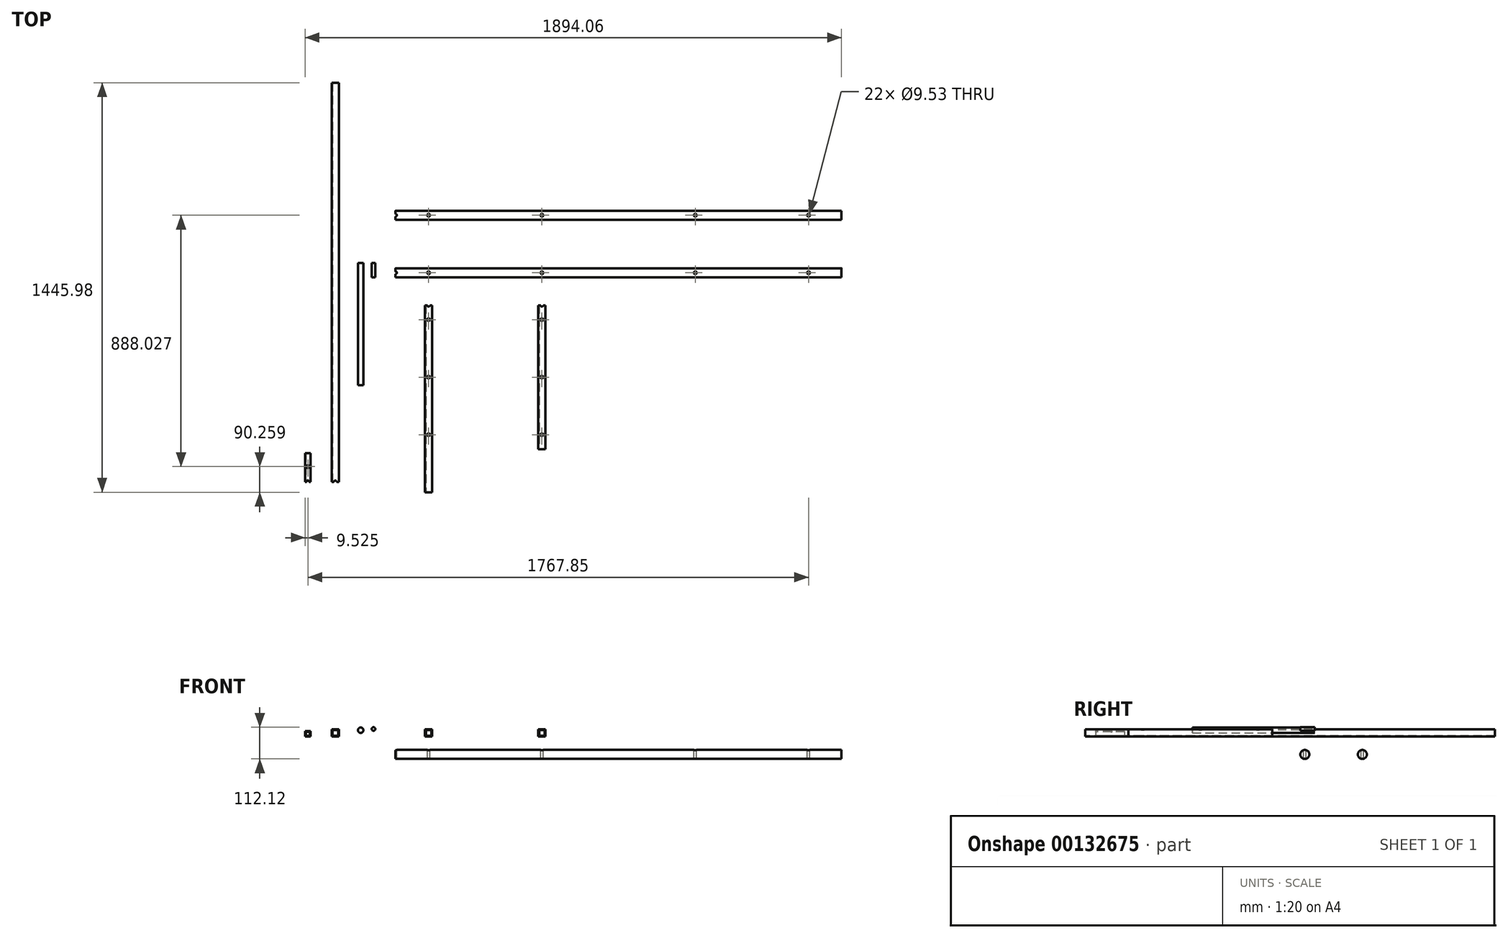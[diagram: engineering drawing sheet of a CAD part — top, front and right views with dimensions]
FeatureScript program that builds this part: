
annotation { "Feature Type Name" : "Feature", "Feature Type Description" : "" }
export const myFeature = defineFeature(function(context is Context, id is Id, definition is map)
    precondition{}
    {
        {
            var Q0;
            Q0=qCreatedBy(makeId("Right.planeOp"),FACE);
            var sketch = newSketch(context, id + "F0", { "sketchPlane" : qUnion([Q0])});
            skCircle(sketch, "E0", {"center": v(-35.07, -63.12) * mm, "radius": 15.88 * mm});
            skCircle(sketch, "E1", {"center": v(168.13, -63.12) * mm, "radius": 15.88 * mm});
            skSolve(sketch);
        }
        {
            var Q0;
            Q0=makeQuery(id+"F0.imprint","IMPRINT",FACE,{"disambiguationData":[TD([[makeQuery(id+"F0.imprint","IMPRINT",EDGE,{"derivedFrom":sQuery(id+"F0.wireOp",EDGE,"E1")}),1.0]])]});
            var Q1;
            Q1=makeQuery(id+"F0.imprint","IMPRINT",FACE,{"disambiguationData":[TD([[makeQuery(id+"F0.imprint","IMPRINT",EDGE,{"derivedFrom":sQuery(id+"F0.wireOp",EDGE,"E0")}),1.0]])]});
            extrude(context, id + "F1", {"entities" : qUnion([Q0, Q1]), "depth" : 1574.8 * mm});
        }
        {
            var Q0;
            Q0=qCreatedBy(makeId("Top.planeOp"),FACE);
            var sketch = newSketch(context, id + "F2", { "sketchPlane" : qUnion([Q0])});
            skPoint(sketch, "E2", {"position": v(0, -35.07) * mm});
            skPoint(sketch, "E3", {"position": v(116.68, -35.07) * mm});
            skPoint(sketch, "E4", {"position": v(1458.12, -35.07) * mm});
            skPoint(sketch, "E5", {"position": v(516.73, -35.07) * mm});
            skPoint(sketch, "E6", {"position": v(1058.07, -35.07) * mm});
            skPoint(sketch, "E7", {"position": v(116.68, 168.13) * mm});
            skPoint(sketch, "E8", {"position": v(0, 168.13) * mm});
            skPoint(sketch, "E9", {"position": v(516.73, 168.13) * mm});
            skPoint(sketch, "E10", {"position": v(1058.07, 168.13) * mm});
            skPoint(sketch, "E11", {"position": v(1458.12, 168.13) * mm});
            skSolve(sketch);
        }
        {
            var Q0;
            Q0=sQuery(id+"F2.wireOp",VERTEX,"E3");
            var Q1;
            Q1=sQuery(id+"F2.wireOp",VERTEX,"E4");
            var Q2;
            Q2=sQuery(id+"F2.wireOp",VERTEX,"E5");
            var Q3;
            Q3=sQuery(id+"F2.wireOp",VERTEX,"E6");
            var Q4;
            Q4=sQuery(id+"F2.wireOp",VERTEX,"E7");
            var Q5;
            Q5=sQuery(id+"F2.wireOp",VERTEX,"E9");
            var Q6;
            Q6=sQuery(id+"F2.wireOp",VERTEX,"E10");
            var Q7;
            Q7=sQuery(id+"F2.wireOp",VERTEX,"E11");
            var Q8;
            Q8=sQuery(id+"F2.wireOp",VERTEX,"E8");
            var Q9;
            Q9=sQuery(id+"F2.wireOp",VERTEX,"E2");
            var Q10;
            Q10=makeQuery(id+"F1.opExtrude","SWEPT_BODY",BODY,{"disambiguationData":[OSD([sQuery(id+"F0.wireOp",EDGE,"E0")])]});
            var Q11;
            Q11=makeQuery(id+"F1.opExtrude","SWEPT_BODY",BODY,{"disambiguationData":[OSD([sQuery(id+"F0.wireOp",EDGE,"E1")])]});
            hole(context, id + "F3", {"style" : HoleStyle.SIMPLE, "endStyle" : HoleEndStyle.THROUGH, "holeDiameter" : 9.52 * mm, "startFromSketch" : true, "locations" : qUnion([Q0, Q1, Q2, Q3, Q4, Q5, Q6, Q7, Q8, Q9]), "scope" : qUnion([Q10, Q11]), "isTappedThrough" : true});
        }
        {
            var Q0;
            Q0=qCreatedBy(makeId("Top.planeOp"),FACE);
            var sketch = newSketch(context, id + "F4", { "sketchPlane" : qUnion([Q0])});
            skLineSegment(sketch, "E12.bottom", {"start": v(103.98, -149.76) * mm, "end": v(129.38, -149.76) * mm});
            skLineSegment(sketch, "E12.top", {"start": v(103.98, -810.16) * mm, "end": v(129.38, -810.16) * mm});
            skLineSegment(sketch, "E12.left", {"start": v(103.98, -149.76) * mm, "end": v(103.98, -810.16) * mm});
            skLineSegment(sketch, "E12.right", {"start": v(129.38, -149.76) * mm, "end": v(129.38, -810.16) * mm});
            skPoint(sketch, "E13", {"position": v(116.68, -149.76) * mm});
            skLineSegment(sketch, "E14.bottom", {"start": v(504.03, -149.76) * mm, "end": v(529.43, -149.76) * mm});
            skLineSegment(sketch, "E14.top", {"start": v(504.03, -657.76) * mm, "end": v(529.43, -657.76) * mm});
            skLineSegment(sketch, "E14.left", {"start": v(504.03, -149.76) * mm, "end": v(504.03, -657.76) * mm});
            skLineSegment(sketch, "E14.right", {"start": v(529.43, -149.76) * mm, "end": v(529.43, -657.76) * mm});
            skPoint(sketch, "E15", {"position": v(516.73, -149.76) * mm});
            skPoint(sketch, "E16", {"position": v(116.68, -200.56) * mm});
            skPoint(sketch, "E17", {"position": v(116.68, -403.76) * mm});
            skPoint(sketch, "E18", {"position": v(116.68, -606.96) * mm});
            skPoint(sketch, "E19", {"position": v(516.73, -200.56) * mm});
            skPoint(sketch, "E20", {"position": v(516.73, -403.76) * mm});
            skPoint(sketch, "E21", {"position": v(516.73, -606.96) * mm});
            skSolve(sketch);
        }
        {
            var Q0;
            Q0=makeQuery(id+"F4.imprint","IMPRINT",FACE,{"disambiguationData":[TD([[makeQuery(id+"F4.imprint","IMPRINT",EDGE,{"derivedFrom":sQuery(id+"F4.wireOp",EDGE,"E12.bottom")}),-1.0]])]});
            extrude(context, id + "F5", {"entities" : qUnion([Q0]), "depth" : 25.4 * mm});
        }
        {
            var Q0;
            Q0=makeQuery(id+"F4.imprint","IMPRINT",FACE,{"disambiguationData":[TD([[makeQuery(id+"F4.imprint","IMPRINT",EDGE,{"derivedFrom":sQuery(id+"F4.wireOp",EDGE,"E14.bottom")}),-1.0]])]});
            extrude(context, id + "F6", {"entities" : qUnion([Q0]), "depth" : 25.4 * mm});
        }
        {
            var Q0;
            Q0=makeQuery(id+"F5.opExtrude","SWEPT_FACE",FACE,{"disambiguationData":[OSD([sQuery(id+"F4.wireOp",EDGE,"E12.top")])]});
            var sketch = newSketch(context, id + "F7", { "sketchPlane" : qUnion([Q0])});
            skLineSegment(sketch, "E22.bottom", {"start": v(106.78, 22.6) * mm, "end": v(126.59, 22.6) * mm});
            skLineSegment(sketch, "E22.top", {"start": v(106.78, 2.8) * mm, "end": v(126.59, 2.8) * mm});
            skLineSegment(sketch, "E22.left", {"start": v(106.78, 22.6) * mm, "end": v(106.78, 2.8) * mm});
            skLineSegment(sketch, "E22.right", {"start": v(126.59, 22.6) * mm, "end": v(126.59, 2.8) * mm});
            skLineSegment(sketch, "E23.bottom", {"start": v(506.83, 22.6) * mm, "end": v(526.64, 22.6) * mm});
            skLineSegment(sketch, "E23.top", {"start": v(506.83, 2.8) * mm, "end": v(526.64, 2.8) * mm});
            skLineSegment(sketch, "E23.left", {"start": v(506.83, 22.6) * mm, "end": v(506.83, 2.8) * mm});
            skLineSegment(sketch, "E23.right", {"start": v(526.64, 22.6) * mm, "end": v(526.64, 2.8) * mm});
            skSolve(sketch);
        }
        {
            var Q0;
            Q0=makeQuery(id+"F7.imprint","IMPRINT",FACE,{"disambiguationData":[TD([[makeQuery(id+"F7.imprint","IMPRINT",EDGE,{"derivedFrom":sQuery(id+"F7.wireOp",EDGE,"E22.bottom")}),-1.0]])]});
            extrude(context, id + "F8", {"entities" : qUnion([Q0]), "operationType" : NewBodyOperationType.REMOVE, "oppositeDirection" : true, "depth" : 660.4 * mm});
        }
        {
            var Q0;
            Q0=makeQuery(id+"F7.imprint","IMPRINT",FACE,{"disambiguationData":[TD([[makeQuery(id+"F7.imprint","IMPRINT",EDGE,{"derivedFrom":sQuery(id+"F7.wireOp",EDGE,"E23.bottom")}),-1.0]])]});
            extrude(context, id + "F9", {"entities" : qUnion([Q0]), "operationType" : NewBodyOperationType.REMOVE, "oppositeDirection" : true, "depth" : 660.4 * mm});
        }
        {
            var Q0;
            Q0=sQuery(id+"F4.wireOp",VERTEX,"E13");
            var Q1;
            Q1=sQuery(id+"F4.wireOp",VERTEX,"E16");
            var Q2;
            Q2=sQuery(id+"F4.wireOp",VERTEX,"E17");
            var Q3;
            Q3=sQuery(id+"F4.wireOp",VERTEX,"E18");
            var Q4;
            Q4=makeQuery(id+"F5.opExtrude","SWEPT_BODY",BODY,{"disambiguationData":[OSD([sQuery(id+"F4.wireOp",EDGE,"E12.bottom"),sQuery(id+"F4.wireOp",EDGE,"E12.top"),sQuery(id+"F4.wireOp",EDGE,"E12.left"),sQuery(id+"F4.wireOp",EDGE,"E12.right")])]});
            hole(context, id + "F10", {"style" : HoleStyle.SIMPLE, "endStyle" : HoleEndStyle.THROUGH, "oppositeDirection" : true, "holeDiameter" : 9.52 * mm, "startFromSketch" : true, "locations" : qUnion([Q0, Q1, Q2, Q3]), "scope" : qUnion([Q4]), "isTappedThrough" : true});
        }
        {
            var Q0;
            Q0=sQuery(id+"F4.wireOp",VERTEX,"E15");
            var Q1;
            Q1=sQuery(id+"F4.wireOp",VERTEX,"E19");
            var Q2;
            Q2=sQuery(id+"F4.wireOp",VERTEX,"E20");
            var Q3;
            Q3=sQuery(id+"F4.wireOp",VERTEX,"E21");
            var Q4;
            Q4=makeQuery(id+"F6.opExtrude","SWEPT_BODY",BODY,{"disambiguationData":[OSD([sQuery(id+"F4.wireOp",EDGE,"E14.bottom"),sQuery(id+"F4.wireOp",EDGE,"E14.top"),sQuery(id+"F4.wireOp",EDGE,"E14.left"),sQuery(id+"F4.wireOp",EDGE,"E14.right")])]});
            hole(context, id + "F11", {"style" : HoleStyle.SIMPLE, "endStyle" : HoleEndStyle.THROUGH, "oppositeDirection" : true, "holeDiameter" : 9.52 * mm, "startFromSketch" : true, "locations" : qUnion([Q0, Q1, Q2, Q3]), "scope" : qUnion([Q4]), "isTappedThrough" : true});
        }
        {
            var Q0;
            Q0=qCreatedBy(makeId("Top.planeOp"),FACE);
            var sketch = newSketch(context, id + "F12", { "sketchPlane" : qUnion([Q0])});
            skLineSegment(sketch, "E24.bottom", {"start": v(-200.05, 635.82) * mm, "end": v(-225.45, 635.82) * mm});
            skLineSegment(sketch, "E24.top", {"start": v(-200.05, -773.88) * mm, "end": v(-225.45, -773.88) * mm});
            skLineSegment(sketch, "E24.left", {"start": v(-200.05, 635.82) * mm, "end": v(-200.05, -773.88) * mm});
            skLineSegment(sketch, "E24.right", {"start": v(-225.45, 635.82) * mm, "end": v(-225.45, -773.88) * mm});
            skLineSegment(sketch, "E25.bottom", {"start": v(-319.26, -672.28) * mm, "end": v(-300.21, -672.28) * mm});
            skLineSegment(sketch, "E25.top", {"start": v(-319.26, -773.88) * mm, "end": v(-300.21, -773.88) * mm});
            skLineSegment(sketch, "E25.left", {"start": v(-319.26, -672.28) * mm, "end": v(-319.26, -773.88) * mm});
            skLineSegment(sketch, "E25.right", {"start": v(-300.21, -672.28) * mm, "end": v(-300.21, -773.88) * mm});
            skSolve(sketch);
        }
        {
            var Q0;
            Q0=makeQuery(id+"F12.imprint","IMPRINT",FACE,{"disambiguationData":[TD([[makeQuery(id+"F12.imprint","IMPRINT",EDGE,{"derivedFrom":sQuery(id+"F12.wireOp",EDGE,"E24.bottom")}),1.0]])]});
            extrude(context, id + "F13", {"entities" : qUnion([Q0]), "depth" : 25.4 * mm});
        }
        {
            var Q0;
            Q0=makeQuery(id+"F12.imprint","IMPRINT",FACE,{"disambiguationData":[TD([[makeQuery(id+"F12.imprint","IMPRINT",EDGE,{"derivedFrom":sQuery(id+"F12.wireOp",EDGE,"E25.bottom")}),-1.0]])]});
            extrude(context, id + "F14", {"entities" : qUnion([Q0]), "depth" : 19.05 * mm});
        }
        {
            var Q0;
            Q0=makeQuery(id+"F13.opExtrude","SWEPT_FACE",FACE,{"disambiguationData":[OSD([sQuery(id+"F12.wireOp",EDGE,"E24.top")])]});
            var sketch = newSketch(context, id + "F15", { "sketchPlane" : qUnion([Q0])});
            skLineSegment(sketch, "E26.bottom", {"start": v(-222.65, 22.6) * mm, "end": v(-202.84, 22.6) * mm});
            skLineSegment(sketch, "E26.top", {"start": v(-222.65, 2.8) * mm, "end": v(-202.84, 2.8) * mm});
            skLineSegment(sketch, "E26.left", {"start": v(-222.65, 22.6) * mm, "end": v(-222.65, 2.8) * mm});
            skLineSegment(sketch, "E26.right", {"start": v(-202.84, 22.6) * mm, "end": v(-202.84, 2.8) * mm});
            skLineSegment(sketch, "E27.bottom", {"start": v(-316.72, 16.51) * mm, "end": v(-302.75, 16.51) * mm});
            skLineSegment(sketch, "E27.top", {"start": v(-316.72, 2.54) * mm, "end": v(-302.75, 2.54) * mm});
            skLineSegment(sketch, "E27.left", {"start": v(-316.72, 16.51) * mm, "end": v(-316.72, 2.54) * mm});
            skLineSegment(sketch, "E27.right", {"start": v(-302.75, 16.51) * mm, "end": v(-302.75, 2.54) * mm});
            skSolve(sketch);
        }
        {
            var Q0;
            Q0=makeQuery(id+"F15.imprint","IMPRINT",FACE,{"disambiguationData":[TD([[makeQuery(id+"F15.imprint","IMPRINT",EDGE,{"derivedFrom":sQuery(id+"F15.wireOp",EDGE,"E26.bottom")}),-1.0]])]});
            extrude(context, id + "F16", {"entities" : qUnion([Q0]), "operationType" : NewBodyOperationType.REMOVE, "oppositeDirection" : true, "depth" : 1409.7 * mm});
        }
        {
            var Q0;
            Q0=makeQuery(id+"F15.imprint","IMPRINT",FACE,{"disambiguationData":[TD([[makeQuery(id+"F15.imprint","IMPRINT",EDGE,{"derivedFrom":sQuery(id+"F15.wireOp",EDGE,"E27.bottom")}),-1.0]])]});
            extrude(context, id + "F17", {"entities" : qUnion([Q0]), "operationType" : NewBodyOperationType.REMOVE, "oppositeDirection" : true, "depth" : 101.6 * mm});
        }
        {
            var Q0;
            Q0=makeQuery(id+"F14.opExtrude","CAP_FACE",FACE,{"disambiguationData":[OSD([sQuery(id+"F12.wireOp",EDGE,"E25.bottom"),sQuery(id+"F12.wireOp",EDGE,"E25.top"),sQuery(id+"F12.wireOp",EDGE,"E25.left"),sQuery(id+"F12.wireOp",EDGE,"E25.right")])],"isStart":false});
            var sketch = newSketch(context, id + "F18", { "sketchPlane" : qUnion([Q0])});
            skPoint(sketch, "E28", {"position": v(-309.74, -773.88) * mm});
            skPoint(sketch, "E29", {"position": v(-309.74, -719.9) * mm});
            skSolve(sketch);
        }
        {
            var Q0;
            Q0=sQuery(id+"F18.wireOp",VERTEX,"E29");
            var Q1;
            Q1=sQuery(id+"F18.wireOp",VERTEX,"E28");
            var Q2;
            Q2=makeQuery(id+"F14.opExtrude","SWEPT_BODY",BODY,{"disambiguationData":[OSD([sQuery(id+"F12.wireOp",EDGE,"E25.bottom"),sQuery(id+"F12.wireOp",EDGE,"E25.top"),sQuery(id+"F12.wireOp",EDGE,"E25.left"),sQuery(id+"F12.wireOp",EDGE,"E25.right")])]});
            hole(context, id + "F19", {"style" : HoleStyle.SIMPLE, "endStyle" : HoleEndStyle.THROUGH, "holeDiameter" : 9.52 * mm, "startFromSketch" : true, "locations" : qUnion([Q0, Q1]), "scope" : qUnion([Q2]), "isTappedThrough" : true});
        }
        {
            var Q0;
            Q0=makeQuery(id+"F13.opExtrude","CAP_FACE",FACE,{"disambiguationData":[OSD([sQuery(id+"F12.wireOp",EDGE,"E24.bottom"),sQuery(id+"F12.wireOp",EDGE,"E24.top"),sQuery(id+"F12.wireOp",EDGE,"E24.left"),sQuery(id+"F12.wireOp",EDGE,"E24.right")])],"isStart":false});
            var sketch = newSketch(context, id + "F20", { "sketchPlane" : qUnion([Q0])});
            skPoint(sketch, "E30", {"position": v(-212.75, -773.88) * mm});
            skSolve(sketch);
        }
        {
            var Q0;
            Q0=sQuery(id+"F20.wireOp",VERTEX,"E30");
            var Q1;
            Q1=makeQuery(id+"F13.opExtrude","SWEPT_BODY",BODY,{"disambiguationData":[OSD([sQuery(id+"F12.wireOp",EDGE,"E24.bottom"),sQuery(id+"F12.wireOp",EDGE,"E24.top"),sQuery(id+"F12.wireOp",EDGE,"E24.left"),sQuery(id+"F12.wireOp",EDGE,"E24.right")])]});
            hole(context, id + "F21", {"style" : HoleStyle.SIMPLE, "endStyle" : HoleEndStyle.THROUGH, "holeDiameter" : 9.52 * mm, "startFromSketch" : true, "locations" : qUnion([Q0]), "scope" : qUnion([Q1]), "isTappedThrough" : true});
        }
        {
            var Q0;
            Q0=qCreatedBy(makeId("Front.planeOp"),FACE);
            var sketch = newSketch(context, id + "F22", { "sketchPlane" : qUnion([Q0])});
            skCircle(sketch, "E31", {"center": v(-123.27, 22.47) * mm, "radius": 9.53 * mm});
            skSolve(sketch);
        }
        {
            var Q0;
            Q0=makeQuery(id+"F22.imprint","IMPRINT",FACE,{"disambiguationData":[TD([[makeQuery(id+"F22.imprint","IMPRINT",EDGE,{"derivedFrom":sQuery(id+"F22.wireOp",EDGE,"E31")}),1.0]])]});
            extrude(context, id + "F23", {"entities" : qUnion([Q0]), "depth" : 431.8 * mm});
        }
        {
            var Q0;
            Q0=qCreatedBy(makeId("Front.planeOp"),FACE);
            var sketch = newSketch(context, id + "F24", { "sketchPlane" : qUnion([Q0])});
            skCircle(sketch, "E32", {"center": v(-77.92, 26.77) * mm, "radius": 6.35 * mm});
            skSolve(sketch);
        }
        {
            var Q0;
            Q0=makeQuery(id+"F24.imprint","IMPRINT",FACE,{"disambiguationData":[TD([[makeQuery(id+"F24.imprint","IMPRINT",EDGE,{"derivedFrom":sQuery(id+"F24.wireOp",EDGE,"E32")}),1.0]])]});
            extrude(context, id + "F25", {"entities" : qUnion([Q0]), "depth" : 50.8 * mm});
        }
    });
